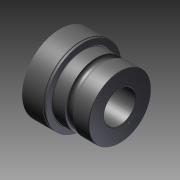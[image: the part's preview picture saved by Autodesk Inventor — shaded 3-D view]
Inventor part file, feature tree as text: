
AUTODESK INVENTOR PART (.ipt)
format: ipt  version: 2011 SP1 (Build 150282100, 282)  size: 219,136 bytes
history: native  units: mm
features: other x7, revolve x1, sketch x1
ambient origin geometry x8: Origin, YZ Plane, XZ Plane, XY Plane, X Axis, Y Axis, Z Axis, Center Point
bodies: Solid1 (feature_tree)
feature tree (9):
  revolve  "Revolution1"  [1 undecoded]
  other  "to_housing_XY"
  other  "to_housing_YZ"
  other  "to_housing_ZX"
  other  "to_housing_X"
  other  "to_housing_Y"
  other  "to_housing_Z"
  other  "to_housing_Center"
  sketch  "Sketch_1"  dims[d0=360.0deg d1=0.0mm]
note: 1 required parameter value undecoded (feature->parameter linkage not recoverable at this tier; creation-order binding heuristic only, values carry confidence <= 0.55)
